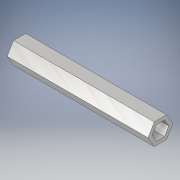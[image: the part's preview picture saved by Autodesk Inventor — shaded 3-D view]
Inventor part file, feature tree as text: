
AUTODESK INVENTOR PART (.ipt)
format: ipt  version: 2018 (Build 220112000, 112)  size: 105,472 bytes
history: native  units: in
note: dims shown in document units (in); Inventor stores cm internally (conversion verified against a paired STEP export)
features: extrude x1, sketch x1
ambient origin geometry x8: Origin, YZ Plane, XZ Plane, XY Plane, X Axis, Y Axis, Z Axis, Center Point
bodies: Solid1 (feature_tree)
feature tree (2):
  extrude  "Extrusion1"  Depth=1.0in TaperAngle=0.0deg
  sketch  "Sketch1"  dims[d0=0.059in d1=1.0in d2=0.0in]
